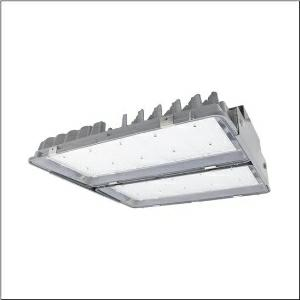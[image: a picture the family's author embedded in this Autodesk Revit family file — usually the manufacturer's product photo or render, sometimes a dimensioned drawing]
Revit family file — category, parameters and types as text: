
# Revit family: highbay_11xtreme_51hf61db4tma
name_source: partatom
category: Lighting Fixtures
units: mm (PartAtom-declared; Revit-internal decimal feet)

## family parameters
Cut with Voids When Loaded = No
Host = Face
Light Source = No
Part Type = Normal
Room Calculation Point = No
Round Connector Dimension = Use Diameter
Shared = No

## types (1)
- --- (1 x LED, 54000 lm, 282.6 W, 4000K)
    Apparent Load = 283 VA
    CIE Flux Codes = 88 96 99 100 100
    Color Rendering = 80
    Color Temperature = 4000K
    Default Elevation = 1800 mm
    Description = Highbay 11Xtreme, high bay luminaire, primary light control with lens, of PMMA, primary optical cover: cover, of toughened safety glass, light emission: direct distribution, primary light characteristic: symmetric, installation type: suspended mounting, surface-mounted, 2x LED module,for 1x 2x LED, rated luminous flux: 54.000lm, luminous efficacy: 191lm/W, light colour: 840, colour temperature: 4000K, control gear: DALI 2, with cable H07RN-F 5x 1.5mm², mains connection: 220..240V, AC, 50/60Hz, cable length: 1,5m, rated input power: 283W, luminaire housing, of diecast aluminium, coated, silver, length: 595mm, width: 560mm, height: 195mm, protection rating (complete): IP66, insulation class (complete): insulation class I (protective earthing), certification: CE, ENEC, UKCA, protection symbol: D, ball protection: ball impact resistant according to DIN VDE 0710 part 13 (with chain suspension), impact resistance: IK08, permissible operating ambient temperature: -25..+60°C, reducing of maximum allowable ambient temperature of 5°C with ceiling mounting, packaging unit: 1 piece
    Height = 157 mm
    Lamp = 1 x LED
    Lamp Light Flux = 54000 lm
    Lamp Power = 282.6 W
    Lamp count = 1
    Length = 593 mm
    Luminous efficacy = 191 lm/W
    Manufacturer = Siteco
    ModVariant = No
    Model = 51HF61DB4TMA
    Mounting Place = Ceiling
    Mounting Type = Pendant
    Number of Poles = 1
    OnlyDefault = Yes
    Power Factor = 1
    Product Name = Highbay 11Xtreme
    Product group = high bay luminaire
    ProductGroupID = 901
    Protection Class = Protection class I
    Protection Degree = IP 66
    RLX_Detail_Level = 1
    RLX_Emergency_Light_Flux = 0 lm
    RLX_Emergency_Type = 0
    RLX_Emergency_Type_DB = No
    RlxData = <blob elided: 33841 chars, md5=4ca7c9ee>
    Socket = socket
    Standby Power = 0 W
    System Light Flux = 53999 lm
    System Power = 283 W
    Type Comments = factory setting: luminous flux: 100 % | dim-lin: 254 | 960 mA
    Type Image = l_1258340.jpg
    URL = http://relux.com
    VarID = @adj_105005
    Voltage = 0 V
    Weight = 0.00 kg
    Width = 278 mm

## geometry (parser evidence)
native form markers: Blend x4, Sweep x10
no freeform markers — native parametric forms only
